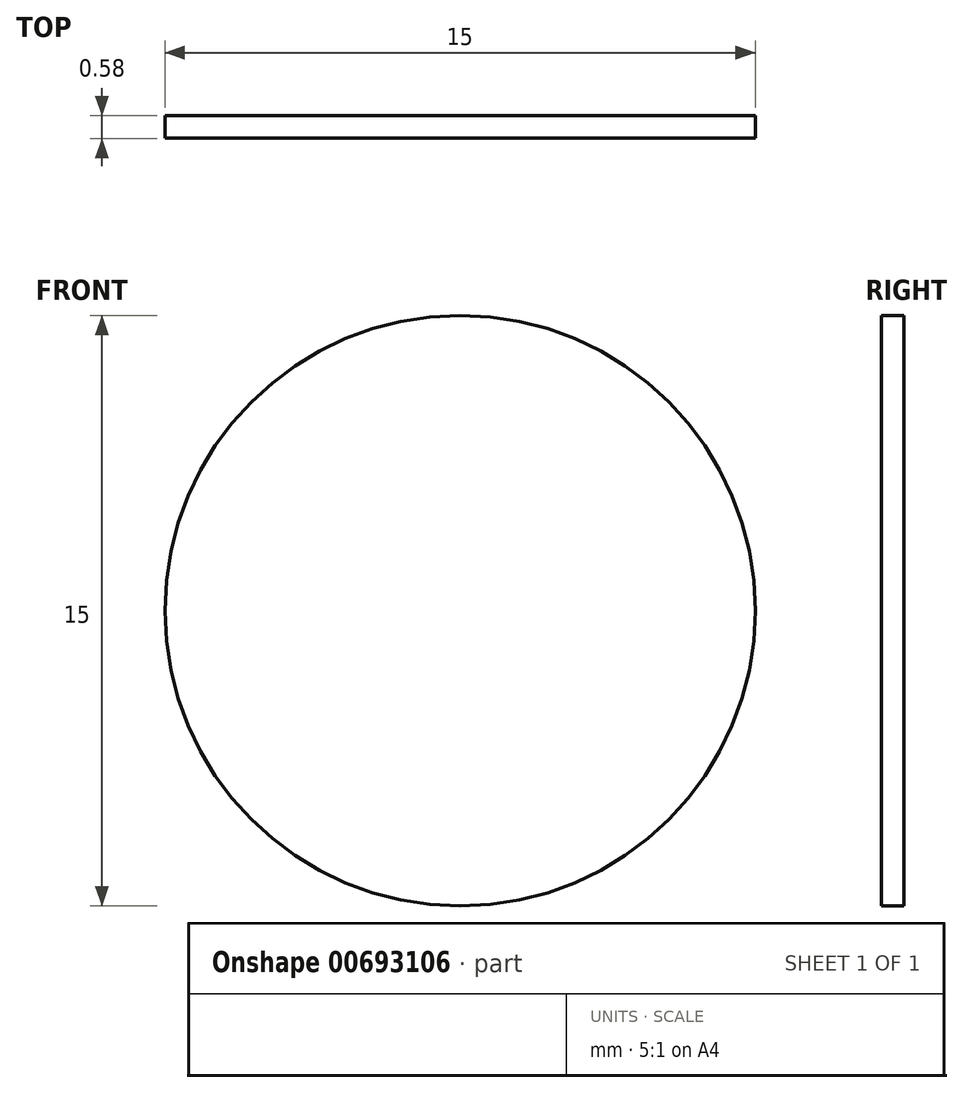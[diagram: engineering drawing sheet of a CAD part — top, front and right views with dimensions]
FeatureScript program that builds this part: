
annotation { "Feature Type Name" : "Feature", "Feature Type Description" : "" }
export const myFeature = defineFeature(function(context is Context, id is Id, definition is map)
    precondition{}
    {
        {
            var Q0;
            Q0=qCreatedBy(makeId("Front.planeOp"),FACE);
            var sketch = newSketch(context, id + "F0", { "sketchPlane" : qUnion([Q0])});
            skCircle(sketch, "E0", {"center": v(0, 0) * mm, "radius": 7.5 * mm});
            skSolve(sketch);
        }
        {
            var Q0;
            Q0=makeQuery(id+"F0.imprint","IMPRINT",FACE,{"disambiguationData":[TD([[makeQuery(id+"F0.imprint","IMPRINT",EDGE,{"derivedFrom":sQuery(id+"F0.wireOp",EDGE,"E0")}),1.0]])]});
            extrude(context, id + "F1", {"entities" : qUnion([Q0]), "depth" : 0.57 * mm, "offsetDistance" : 25 * mm});
        }
    });
